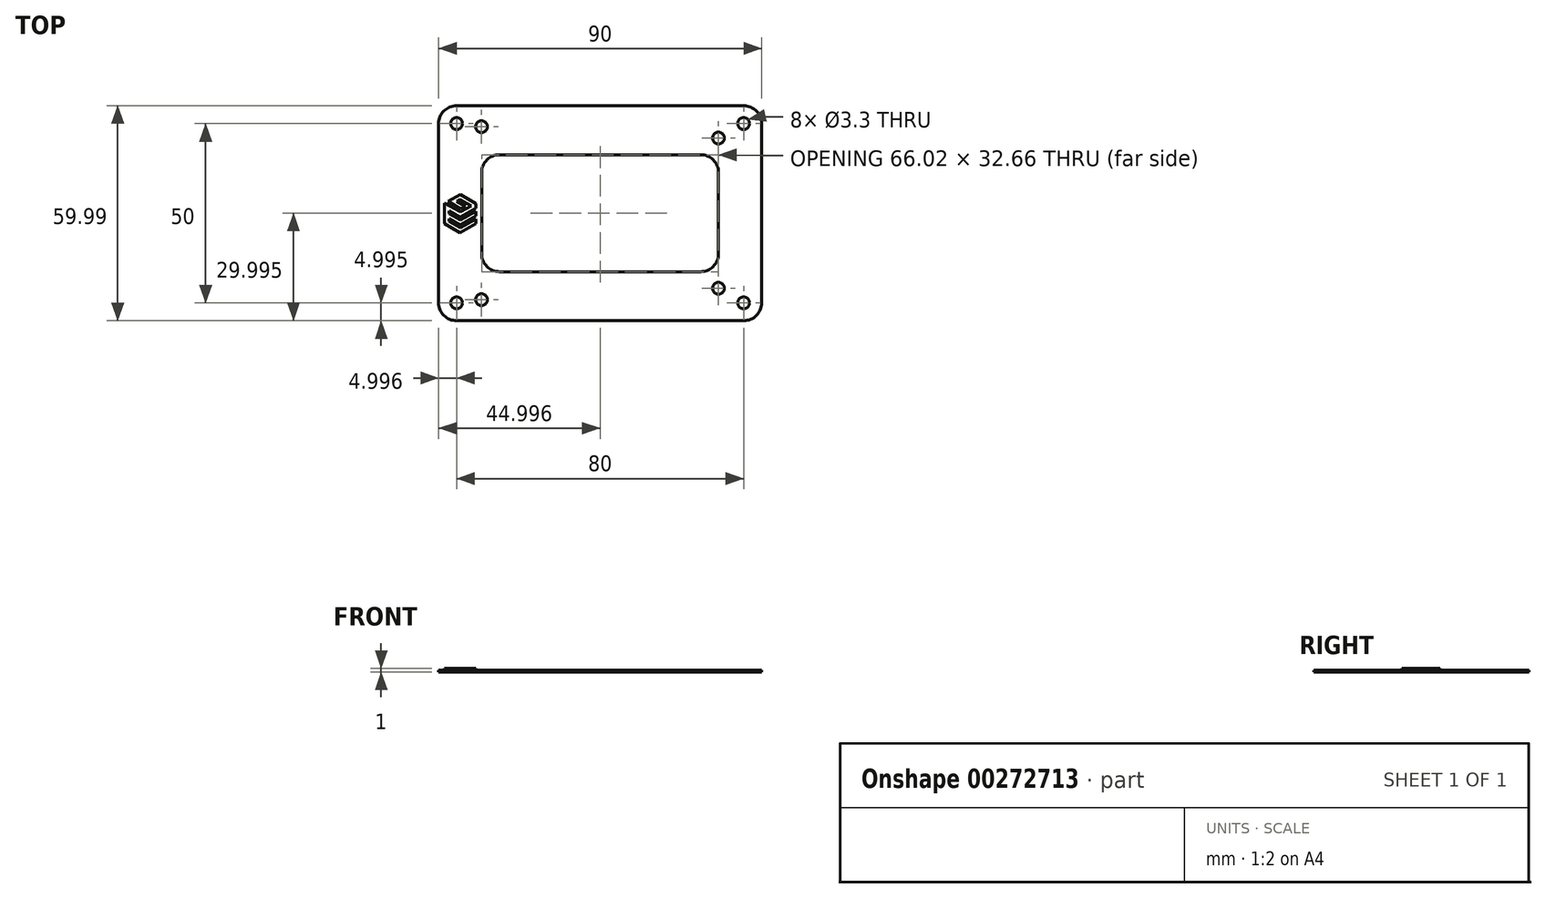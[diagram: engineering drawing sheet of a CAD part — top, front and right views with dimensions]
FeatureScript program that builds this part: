
annotation { "Feature Type Name" : "Feature", "Feature Type Description" : "" }
export const myFeature = defineFeature(function(context is Context, id is Id, definition is map)
    precondition{}
    {
        {
            var Q0;
            Q0=qCreatedBy(makeId("Top.planeOp"),FACE);
            var sketch = newSketch(context, id + "F0", { "sketchPlane" : qUnion([Q0])});
            skCircle(sketch, "E0", {"center": v(14.6, 3.18) * mm, "radius": 1.65 * mm});
            skCircle(sketch, "E1", {"center": v(14.6, 51.44) * mm, "radius": 1.65 * mm});
            skCircle(sketch, "E2", {"center": v(80.65, 48.26) * mm, "radius": 1.65 * mm});
            skCircle(sketch, "E3", {"center": v(80.65, 6.35) * mm, "radius": 1.65 * mm});
            skLineSegment(sketch, "E4.bottom", {"start": v(87.66, 52.3) * mm, "end": v(7.66, 52.3) * mm});
            skCircle(sketch, "E5", {"center": v(7.66, 52.3) * mm, "radius": 1.65 * mm});
            skCircle(sketch, "E6", {"center": v(87.66, 52.3) * mm, "radius": 1.65 * mm});
            skCircle(sketch, "E7", {"center": v(87.66, 2.3) * mm, "radius": 1.65 * mm});
            skCircle(sketch, "E8", {"center": v(7.66, 2.3) * mm, "radius": 1.65 * mm});
            skLineSegment(sketch, "E9.bottom", {"start": v(87.66, 57.3) * mm, "end": v(7.66, 57.3) * mm});
            skLineSegment(sketch, "E9.top", {"start": v(87.66, -2.7) * mm, "end": v(7.66, -2.7) * mm});
            skLineSegment(sketch, "E9.left", {"start": v(92.66, 52.3) * mm, "end": v(92.66, 2.3) * mm});
            skLineSegment(sketch, "E9.right", {"start": v(2.66, 52.3) * mm, "end": v(2.66, 2.3) * mm});
            skLineSegment(sketch, "E10.bottom", {"start": v(75.67, 43.64) * mm, "end": v(19.65, 43.64) * mm});
            skLineSegment(sketch, "E10.top", {"start": v(75.67, 10.97) * mm, "end": v(19.65, 10.97) * mm});
            skLineSegment(sketch, "E10.left", {"start": v(80.67, 38.64) * mm, "end": v(80.67, 15.97) * mm});
            skLineSegment(sketch, "E10.right", {"start": v(14.65, 38.64) * mm, "end": v(14.65, 15.97) * mm});
            skPoint(sketch, "E10.middle", {"position": v(47.66, 27.3) * mm});
            skPoint(sketch, "E11.visualSharp", {"position": v(2.66, 57.3) * mm});
            skArc(sketch, "E11.filletArc", {"start": v(7.66, 57.3) * mm, "mid": v(4.12, 55.84) * mm, "end": v(2.66, 52.3) * mm});
            skPoint(sketch, "E12.visualSharp", {"position": v(2.66, -2.7) * mm});
            skArc(sketch, "E12.filletArc", {"start": v(2.66, 2.3) * mm, "mid": v(4.12, -1.23) * mm, "end": v(7.66, -2.7) * mm});
            skPoint(sketch, "E13.visualSharp", {"position": v(92.66, -2.7) * mm});
            skArc(sketch, "E13.filletArc", {"start": v(87.66, -2.7) * mm, "mid": v(91.2, -1.23) * mm, "end": v(92.66, 2.3) * mm});
            skPoint(sketch, "E14.visualSharp", {"position": v(92.66, 57.3) * mm});
            skArc(sketch, "E14.filletArc", {"start": v(92.66, 52.3) * mm, "mid": v(91.2, 55.84) * mm, "end": v(87.66, 57.3) * mm});
            skPoint(sketch, "E15.visualSharp", {"position": v(80.67, 43.64) * mm});
            skArc(sketch, "E15.filletArc", {"start": v(80.67, 38.64) * mm, "mid": v(79.2, 42.17) * mm, "end": v(75.67, 43.64) * mm});
            skPoint(sketch, "E16.visualSharp", {"position": v(14.65, 10.97) * mm});
            skArc(sketch, "E16.filletArc", {"start": v(14.65, 15.97) * mm, "mid": v(16.11, 12.44) * mm, "end": v(19.65, 10.97) * mm});
            skPoint(sketch, "E17.visualSharp", {"position": v(80.67, 10.97) * mm});
            skArc(sketch, "E17.filletArc", {"start": v(75.67, 10.97) * mm, "mid": v(79.2, 12.44) * mm, "end": v(80.67, 15.97) * mm});
            skPoint(sketch, "E18.visualSharp", {"position": v(14.65, 43.64) * mm});
            skArc(sketch, "E18.filletArc", {"start": v(19.65, 43.64) * mm, "mid": v(16.11, 42.17) * mm, "end": v(14.65, 38.64) * mm});
            skLineSegment(sketch, "E19", {"start": v(13.06, 25.7) * mm, "end": v(13.06, 24.39) * mm});
            skLineSegment(sketch, "E20", {"start": v(13.06, 24.39) * mm, "end": v(8.65, 21.85) * mm});
            skLineSegment(sketch, "E21", {"start": v(8.65, 21.85) * mm, "end": v(4.25, 24.39) * mm});
            skLineSegment(sketch, "E22", {"start": v(4.25, 24.39) * mm, "end": v(4.25, 30.07) * mm});
            skLineSegment(sketch, "E23", {"start": v(4.25, 30.07) * mm, "end": v(8.68, 27.64) * mm});
            skLineSegment(sketch, "E24", {"start": v(8.68, 27.64) * mm, "end": v(11.75, 29.37) * mm});
            skLineSegment(sketch, "E25", {"start": v(11.75, 29.37) * mm, "end": v(8.65, 31.07) * mm});
            skLineSegment(sketch, "E26", {"start": v(8.65, 31.07) * mm, "end": v(7.71, 30.57) * mm});
            skLineSegment(sketch, "E27", {"start": v(7.71, 30.57) * mm, "end": v(10.07, 29.18) * mm});
            skLineSegment(sketch, "E28", {"start": v(10.07, 29.18) * mm, "end": v(8.81, 28.5) * mm});
            skLineSegment(sketch, "E29", {"start": v(8.81, 28.5) * mm, "end": v(5.3, 30.57) * mm});
            skLineSegment(sketch, "E30", {"start": v(5.3, 30.57) * mm, "end": v(8.68, 32.48) * mm});
            skLineSegment(sketch, "E31", {"start": v(8.68, 32.48) * mm, "end": v(13.06, 29.94) * mm});
            skLineSegment(sketch, "E32", {"start": v(13.06, 29.94) * mm, "end": v(13.06, 28.76) * mm});
            skLineSegment(sketch, "E33", {"start": v(13.06, 28.76) * mm, "end": v(8.65, 26.22) * mm});
            skLineSegment(sketch, "E34", {"start": v(8.65, 26.22) * mm, "end": v(5.56, 27.95) * mm});
            skLineSegment(sketch, "E35", {"start": v(5.56, 27.95) * mm, "end": v(5.56, 27.17) * mm});
            skLineSegment(sketch, "E36", {"start": v(5.56, 27.17) * mm, "end": v(8.68, 25.46) * mm});
            skLineSegment(sketch, "E37", {"start": v(8.68, 25.46) * mm, "end": v(13.06, 27.87) * mm});
            skLineSegment(sketch, "E38", {"start": v(13.06, 27.87) * mm, "end": v(13.06, 26.56) * mm});
            skLineSegment(sketch, "E39", {"start": v(13.06, 26.56) * mm, "end": v(8.65, 24.05) * mm});
            skLineSegment(sketch, "E40", {"start": v(8.65, 24.05) * mm, "end": v(5.56, 25.8) * mm});
            skLineSegment(sketch, "E41", {"start": v(5.56, 25.8) * mm, "end": v(5.56, 25) * mm});
            skLineSegment(sketch, "E42", {"start": v(5.56, 25) * mm, "end": v(8.68, 23.26) * mm});
            skLineSegment(sketch, "E43", {"start": v(8.68, 23.26) * mm, "end": v(13.06, 25.7) * mm});
            skSolve(sketch);
        }
        {
            var Q0;
            Q0=qSketchRegion(id+"F0",true);
            var Q1;
            Q1=makeQuery(id+"F0.imprint","IMPRINT",FACE,{"disambiguationData":[TD([[makeQuery(id+"F0.imprint","IMPRINT",EDGE,{"derivedFrom":sQuery(id+"F0.wireOp",EDGE,"E19")}),-1.0]])]});
            extrude(context, id + "F1", {"entities" : qUnion([Q0, Q1]), "depth" : .5 * mm});
        }
        {
            var Q0;
            Q0=makeQuery(id+"F0.imprint","IMPRINT",FACE,{"disambiguationData":[TD([[makeQuery(id+"F0.imprint","IMPRINT",EDGE,{"derivedFrom":sQuery(id+"F0.wireOp",EDGE,"E19")}),-1.0]])]});
            extrude(context, id + "F2", {"entities" : qUnion([Q0]), "operationType" : NewBodyOperationType.ADD, "depth" : 1 * mm});
        }
    });
